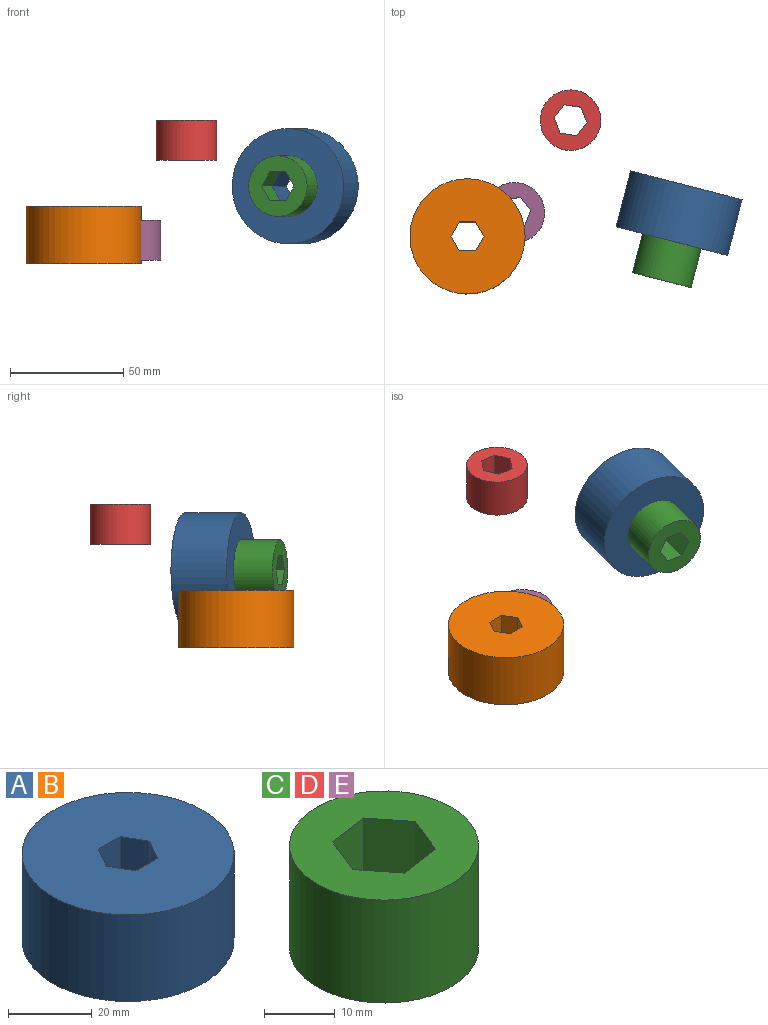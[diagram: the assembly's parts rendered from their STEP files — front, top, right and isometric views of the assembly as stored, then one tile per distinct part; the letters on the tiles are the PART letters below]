
ASSEMBLY  parts=5 mates=1
PART A: 9 faces, bbox 50.8x50.8x25.4 mm
  f0: plane 25.4x6.35mm, normal (-0.87,-0.5,0), area 186.2mm2, adj f1,f5,f7,f8
  f1: plane 25.4x6.35mm, normal (-0.87,0.5,0), area 186.2mm2, adj f0,f2,f7,f8
  f2: plane 25.4x7.33mm, normal (0,1,0), area 186.2mm2, adj f1,f3,f7,f8
  f3: plane 25.4x6.35mm, normal (0.87,0.5,0), area 186.2mm2, adj f2,f4,f7,f8
  f4: plane 25.4x6.35mm, normal (0.87,-0.5,0), area 186.2mm2, adj f3,f5,f7,f8
  f5: plane 25.4x7.33mm, normal (0,-1,0), area 186.2mm2, adj f0,f4,f7,f8
  f6: cylinder r=25.4mm len=50.8mm, axis (0,0,-1), area 4053.7mm2, adj f7,f8
  f7: plane 50.8x50.8mm, normal (0,0,1), area 1887.1mm2, adj f0,f1,f2,f3,f4,f5,f6
  f8: plane 50.8x50.8mm, normal (0,0,-1), area 1887.1mm2, adj f0,f1,f2,f3,f4,f5,f6
PART B: same geometry as A
PART C: 9 faces, bbox 26.7x26.7x17.8 mm
  f0: plane 17.78x5.77mm, normal (-0.79,-0.62,0), area 130.4mm2, adj f1,f5,f7,f8
  f1: plane 17.78x6.81mm, normal (-0.93,0.37,0), area 130.4mm2, adj f0,f2,f7,f8
  f2: plane 17.78x7.26mm, normal (-0.14,0.99,0), area 130.4mm2, adj f1,f3,f7,f8
  f3: plane 17.78x5.77mm, normal (0.79,0.62,0), area 130.4mm2, adj f2,f4,f7,f8
  f4: plane 17.78x6.81mm, normal (0.93,-0.37,0), area 130.4mm2, adj f3,f5,f7,f8
  f5: plane 17.78x7.26mm, normal (0.14,-0.99,0), area 130.4mm2, adj f0,f4,f7,f8
  f6: cylinder r=13.34mm len=26.69mm, axis (0,0,-1), area 1490.5mm2, adj f7,f8
  f7: plane 26.69x26.69mm, normal (0,0,1), area 419.6mm2, adj f0,f1,f2,f3,f4,f5,f6
  f8: plane 26.69x26.69mm, normal (0,0,-1), area 419.6mm2, adj f0,f1,f2,f3,f4,f5,f6
PART D: same geometry as C
PART E: same geometry as C
PLACE A rot(axis=(0.09,0.7,0.7),169.7deg) t=(-71.38,-6.99,4.96)mm
PLACE B t=(-2.78,-76.33,21.92)mm
PLACE C rot(axis=(-0.98,0.05,-0.2),92.4deg) t=(40.39,-54.29,89.03)mm
PLACE D rot(axis=(0,1,0),180deg) t=(-82.03,-0.19,85.31)mm
PLACE E t=(-18.73,-40.98,23.42)mm
MATE revolute A.f6 <-> C.f6  axis (-0.25,-0.97,0) through (6.72,-27.21,56.19)mm
